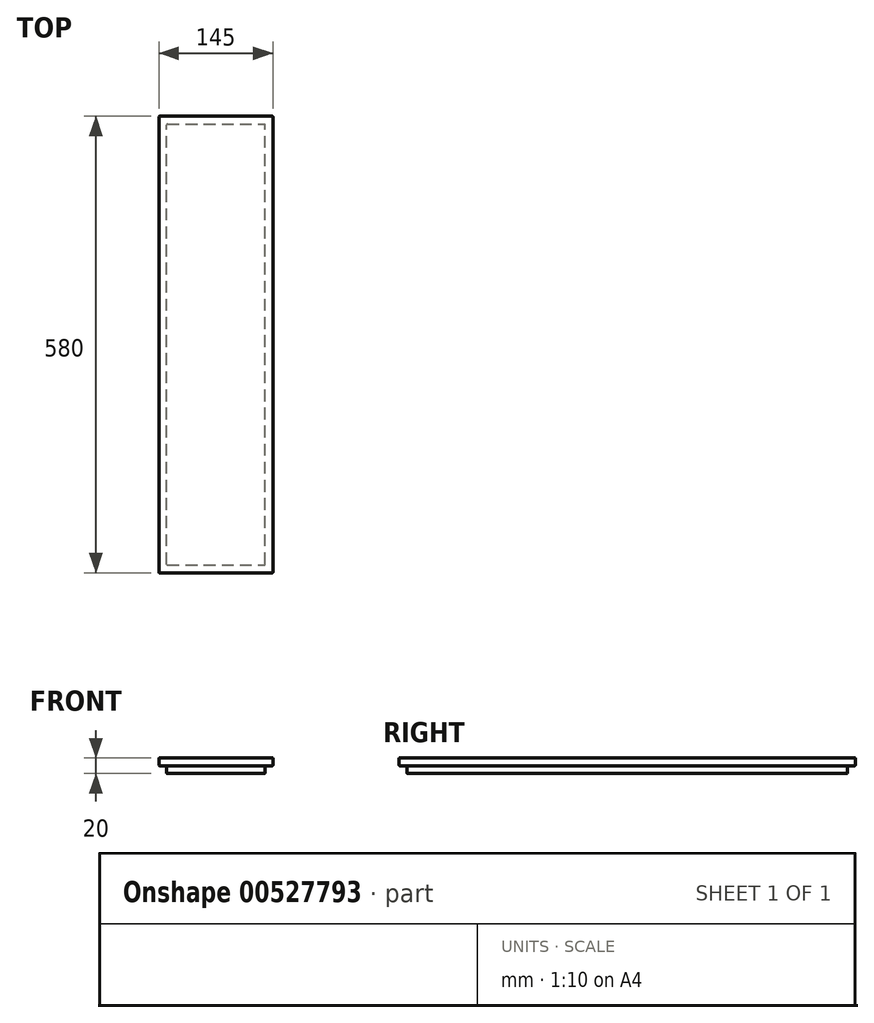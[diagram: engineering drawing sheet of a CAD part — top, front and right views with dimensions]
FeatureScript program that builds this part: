
annotation { "Feature Type Name" : "Feature", "Feature Type Description" : "" }
export const myFeature = defineFeature(function(context is Context, id is Id, definition is map)
    precondition{}
    {
        {
            var Q0;
            Q0=qCreatedBy(makeId("Top.planeOp"),FACE);
            var sketch = newSketch(context, id + "F0", { "sketchPlane" : qUnion([Q0])});
            skLineSegment(sketch, "E0.bottom", {"start": v(-184.62, -285.51) * mm, "end": v(-39.62, -285.51) * mm});
            skLineSegment(sketch, "E0.top", {"start": v(-184.62, 294.49) * mm, "end": v(-39.62, 294.49) * mm});
            skLineSegment(sketch, "E0.left", {"start": v(-184.62, -285.51) * mm, "end": v(-184.62, 294.49) * mm});
            skLineSegment(sketch, "E0.right", {"start": v(-39.62, -285.51) * mm, "end": v(-39.62, 294.49) * mm});
            skSolve(sketch);
        }
        {
            var Q0;
            Q0=qSketchRegion(id+"F0",true);
            extrude(context, id + "F1", {"entities" : qUnion([Q0]), "depth" : 10 * mm, "offsetDistance" : 25 * mm});
        }
        {
            var Q0;
            Q0=makeQuery(id+"F1.opExtrude","CAP_FACE",FACE,{"disambiguationData":[OSD([sQuery(id+"F0.wireOp",EDGE,"E0.bottom"),sQuery(id+"F0.wireOp",EDGE,"E0.top"),sQuery(id+"F0.wireOp",EDGE,"E0.left"),sQuery(id+"F0.wireOp",EDGE,"E0.right")])],"isStart":true});
            var sketch = newSketch(context, id + "F2", { "sketchPlane" : qUnion([Q0])});
            skLineSegment(sketch, "E1.bottom", {"start": v(-174.62, 275.51) * mm, "end": v(-49.62, 275.51) * mm});
            skLineSegment(sketch, "E1.top", {"start": v(-174.62, -284.49) * mm, "end": v(-49.62, -284.49) * mm});
            skLineSegment(sketch, "E1.left", {"start": v(-174.62, 275.51) * mm, "end": v(-174.62, -284.49) * mm});
            skLineSegment(sketch, "E1.right", {"start": v(-49.62, 275.51) * mm, "end": v(-49.62, -284.49) * mm});
            skSolve(sketch);
        }
        {
            var Q0;
            Q0=makeQuery(id+"F2.imprint","IMPRINT",FACE,{"disambiguationData":[TD([[makeQuery(id+"F2.imprint","IMPRINT",EDGE,{"derivedFrom":sQuery(id+"F2.wireOp",EDGE,"E1.bottom")}),-1.0]])]});
            extrude(context, id + "F3", {"entities" : qUnion([Q0]), "operationType" : NewBodyOperationType.ADD, "depth" : 10 * mm, "offsetDistance" : 25 * mm});
        }
        {
            var Q0;
            Q0=makeQuery(id+"F3.opExtrude","CAP_FACE",FACE,{"disambiguationData":[OSD([sQuery(id+"F2.wireOp",EDGE,"E1.bottom"),sQuery(id+"F2.wireOp",EDGE,"E1.top"),sQuery(id+"F2.wireOp",EDGE,"E1.left"),sQuery(id+"F2.wireOp",EDGE,"E1.right")])],"isStart":false});
            var Q1;
            Q1=makeQuery(id+"F1.opExtrude","CAP_EDGE",EDGE,{"disambiguationData":[OSD([sQuery(id+"F0.wireOp",EDGE,"E0.left")])],"isStart":true});
            var Q2;
            Q2=makeQuery(id+"F3.opExtrude","SWEPT_FACE",FACE,{"disambiguationData":[OSD([sQuery(id+"F2.wireOp",EDGE,"E1.bottom")])]});
            var Q3;
            Q3=makeQuery(id+"F3.opExtrude","SWEPT_FACE",FACE,{"disambiguationData":[OSD([sQuery(id+"F2.wireOp",EDGE,"E1.right")])]});
            var Q4;
            Q4=makeQuery(id+"F1.opExtrude","SWEPT_FACE",FACE,{"disambiguationData":[OSD([sQuery(id+"F0.wireOp",EDGE,"E0.right")])]});
            var Q5;
            Q5=makeQuery(id+"F1.opExtrude","SWEPT_FACE",FACE,{"disambiguationData":[OSD([sQuery(id+"F0.wireOp",EDGE,"E0.bottom")])]});
            var Q6;
            Q6=makeQuery(id+"F1.opExtrude","SWEPT_FACE",FACE,{"disambiguationData":[OSD([sQuery(id+"F0.wireOp",EDGE,"E0.left")])]});
            var Q7;
            Q7=makeQuery(id+"F1.opExtrude","SWEPT_FACE",FACE,{"disambiguationData":[OSD([sQuery(id+"F0.wireOp",EDGE,"E0.top")])]});
            var Q8;
            Q8=makeQuery(id+"F3.opExtrude","SWEPT_FACE",FACE,{"disambiguationData":[OSD([sQuery(id+"F2.wireOp",EDGE,"E1.top")])]});
            var Q9;
            Q9=makeQuery(id+"F3.opExtrude","SWEPT_FACE",FACE,{"disambiguationData":[OSD([sQuery(id+"F2.wireOp",EDGE,"E1.left")])]});
            fillet(context, id + "F4", {"entities" : qUnion([Q0, Q1, Q2, Q3, Q4, Q5, Q6, Q7, Q8, Q9]), "radius" : 1 * mm, "tangentPropagation" : true, "allowEdgeOverflow" : false});
        }
    });
